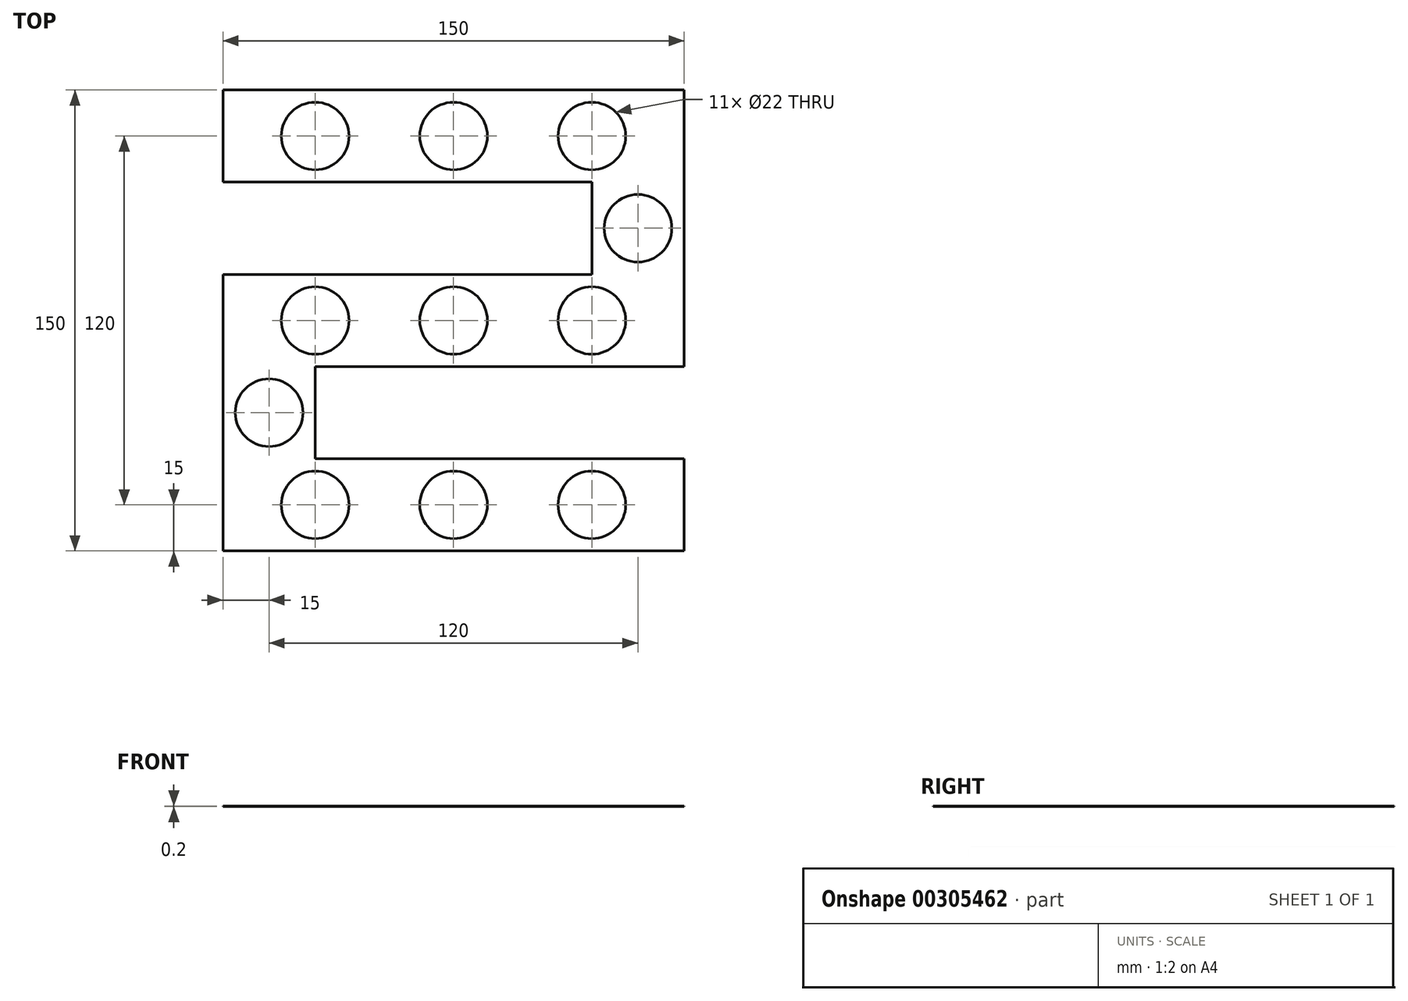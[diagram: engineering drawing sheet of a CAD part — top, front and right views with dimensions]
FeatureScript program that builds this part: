
annotation { "Feature Type Name" : "Feature", "Feature Type Description" : "" }
export const myFeature = defineFeature(function(context is Context, id is Id, definition is map)
    precondition{}
    {
        {
            var Q0;
            Q0=qCreatedBy(makeId("Top.planeOp"),FACE);
            var sketch = newSketch(context, id + "F0", { "sketchPlane" : qUnion([Q0])});
            skLineSegment(sketch, "E0.bottom", {"start": v(150, -150) * mm, "end": v(0, -150) * mm});
            skLineSegment(sketch, "E0.top", {"start": v(150, 0) * mm, "end": v(0, 0) * mm});
            skLineSegment(sketch, "E0.left", {"start": v(150, -150) * mm, "end": v(150, 0) * mm});
            skLineSegment(sketch, "E0.right", {"start": v(0, -150) * mm, "end": v(0, 0) * mm});
            skLineSegment(sketch, "E1.bottom", {"start": v(0, -30) * mm, "end": v(120, -30) * mm});
            skLineSegment(sketch, "E1.top", {"start": v(0, -60) * mm, "end": v(120, -60) * mm});
            skLineSegment(sketch, "E1.left", {"start": v(0, -30) * mm, "end": v(0, -60) * mm});
            skLineSegment(sketch, "E1.right", {"start": v(120, -30) * mm, "end": v(120, -60) * mm});
            skLineSegment(sketch, "E2.bottom", {"start": v(150, -90) * mm, "end": v(30, -90) * mm});
            skLineSegment(sketch, "E2.top", {"start": v(150, -120) * mm, "end": v(30, -120) * mm});
            skLineSegment(sketch, "E2.left", {"start": v(150, -90) * mm, "end": v(150, -120) * mm});
            skLineSegment(sketch, "E2.right", {"start": v(30, -90) * mm, "end": v(30, -120) * mm});
            skLineSegment(sketch, "E3", {"start": v(120, 0) * mm, "end": v(120, -30) * mm, "construction": true});
            skLineSegment(sketch, "E4", {"start": v(120, -60) * mm, "end": v(120, -90) * mm, "construction": true});
            skLineSegment(sketch, "E5", {"start": v(120, -120) * mm, "end": v(120, -150) * mm, "construction": true});
            skLineSegment(sketch, "E6", {"start": v(120, -30) * mm, "end": v(150, -30) * mm, "construction": true});
            skCircle(sketch, "E7", {"center": v(120, -15) * mm, "radius": 11 * mm});
            skPoint(sketch, "E7.centerSnap0", {"position": v(120, -15) * mm});
            skLineSegment(sketch, "E8", {"start": v(75, 0) * mm, "end": v(75, -150) * mm, "construction": true});
            skCircle(sketch, "E9", {"center": v(75, -15) * mm, "radius": 11 * mm});
            skCircle(sketch, "E10", {"center": v(30, -15) * mm, "radius": 11 * mm});
            skLineSegment(sketch, "E11", {"start": v(30, -15) * mm, "end": v(75, -15) * mm, "construction": true});
            skLineSegment(sketch, "E12", {"start": v(75, -15) * mm, "end": v(120, -15) * mm, "construction": true});
            skCircle(sketch, "E13", {"center": v(120, -75) * mm, "radius": 11 * mm});
            skCircle(sketch, "E14", {"center": v(75, -75) * mm, "radius": 11 * mm});
            skCircle(sketch, "E15", {"center": v(30, -75) * mm, "radius": 11 * mm});
            skCircle(sketch, "E16", {"center": v(120, -135) * mm, "radius": 11 * mm});
            skCircle(sketch, "E17", {"center": v(75, -135) * mm, "radius": 11 * mm});
            skCircle(sketch, "E18", {"center": v(30, -135) * mm, "radius": 11 * mm});
            skLineSegment(sketch, "E19", {"start": v(30, -75) * mm, "end": v(75, -75) * mm, "construction": true});
            skLineSegment(sketch, "E20", {"start": v(30, -135) * mm, "end": v(75, -135) * mm, "construction": true});
            skLineSegment(sketch, "E21", {"start": v(120, -45) * mm, "end": v(150, -45) * mm, "construction": true});
            skLineSegment(sketch, "E22", {"start": v(30, -105) * mm, "end": v(0, -105) * mm, "construction": true});
            skPoint(sketch, "E22.endSnap0", {"position": v(30, -105) * mm});
            skCircle(sketch, "E23", {"center": v(135, -45) * mm, "radius": 11 * mm});
            skCircle(sketch, "E24", {"center": v(15, -105) * mm, "radius": 11 * mm});
            skLineSegment(sketch, "E25.bottom", {"start": v(120, -90) * mm, "end": v(150, -90) * mm});
            skLineSegment(sketch, "E25.top", {"start": v(120, -120) * mm, "end": v(150, -120) * mm});
            skLineSegment(sketch, "E25.left", {"start": v(120, -90) * mm, "end": v(120, -120) * mm});
            skLineSegment(sketch, "E26.bottom", {"start": v(0, -30) * mm, "end": v(30, -30) * mm});
            skLineSegment(sketch, "E26.top", {"start": v(0, -60) * mm, "end": v(30, -60) * mm});
            skLineSegment(sketch, "E26.right", {"start": v(30, -30) * mm, "end": v(30, -60) * mm});
            skSolve(sketch);
        }
        {
            var Q0;
            {var subQ6=sQuery(id+"F0.wireOp",EDGE,"E0.bottom");Q0=makeQuery(id+"F0.imprint","IMPRINT",FACE,{"disambiguationData":[TD([[makeQuery(id+"F0.imprint","IMPRINT",EDGE,{"derivedFrom":subQ6}),-1.0]])]});}
            var Q1;
            Q1=makeQuery(id+"F0.imprint","IMPRINT",FACE,{"disambiguationData":[TD([[makeQuery(id+"F0.imprint","IMPRINT",EDGE,{"derivedFrom":sQuery(id+"F0.wireOp",EDGE,"E26.bottom")}),-1.0]])]});
            var Q2;
            Q2=makeQuery(id+"F0.imprint","IMPRINT",FACE,{"disambiguationData":[TD([[makeQuery(id+"F0.imprint","IMPRINT",EDGE,{"derivedFrom":sQuery(id+"F0.wireOp",EDGE,"E25.bottom")}),-1.0]])]});
            extrude(context, id + "F1", {"entities" : qUnion([Q0, Q1, Q2]), "offsetDistance" : 25 * mm, "depth" : .2 * mm});
        }
    });
